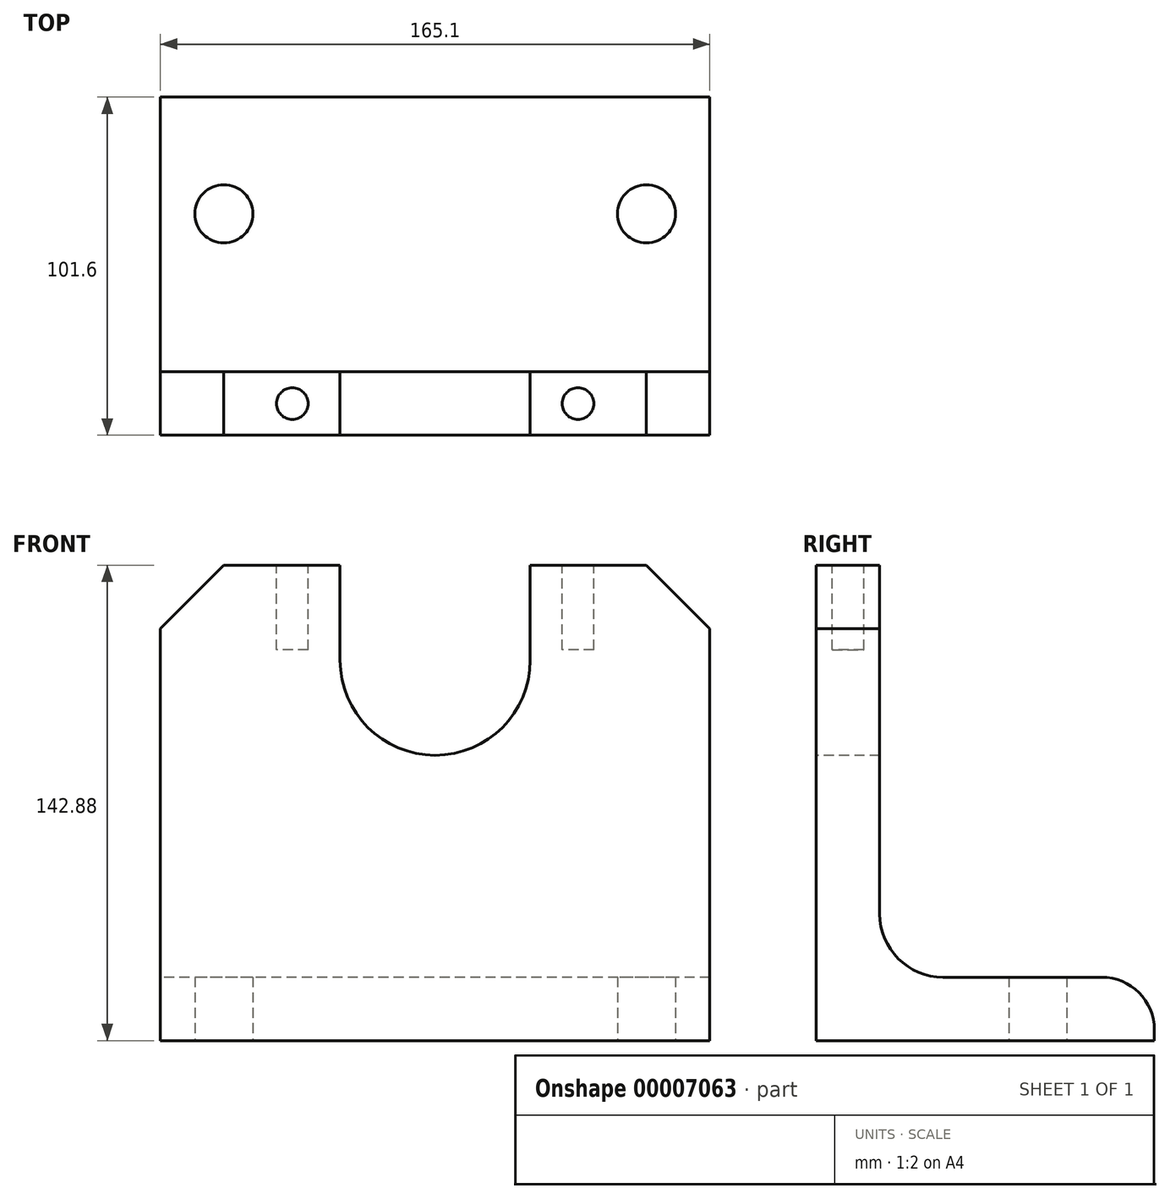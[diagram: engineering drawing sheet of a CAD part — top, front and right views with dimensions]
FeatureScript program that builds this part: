
annotation { "Feature Type Name" : "Feature", "Feature Type Description" : "" }
export const myFeature = defineFeature(function(context is Context, id is Id, definition is map)
    precondition{}
    {
        {
            var Q0;
            Q0=qCreatedBy(makeId("Right.planeOp"),FACE);
            var sketch = newSketch(context, id + "F0", { "sketchPlane" : qUnion([Q0])});
            skLineSegment(sketch, "E0", {"start": v(0, 0) * mm, "end": v(101.6, 0) * mm});
            skLineSegment(sketch, "E1", {"start": v(0, 0) * mm, "end": v(0, 142.88) * mm});
            skLineSegment(sketch, "E2.0", {"start": v(38.1, 19.05) * mm, "end": v(85.73, 19.05) * mm});
            skLineSegment(sketch, "E3.0", {"start": v(19.05, 38.1) * mm, "end": v(19.05, 142.88) * mm});
            skPoint(sketch, "E4.visualSharp", {"position": v(19.05, 19.05) * mm});
            skArc(sketch, "E4.filletArc", {"start": v(19.05, 38.1) * mm, "mid": v(24.63, 24.63) * mm, "end": v(38.1, 19.05) * mm});
            skLineSegment(sketch, "E5", {"start": v(101.6, 0) * mm, "end": v(101.6, 3.18) * mm});
            skArc(sketch, "E6.filletArc", {"start": v(101.6, 3.18) * mm, "mid": v(96.95, 14.4) * mm, "end": v(85.73, 19.05) * mm});
            skLineSegment(sketch, "E7", {"start": v(0, 142.88) * mm, "end": v(19.05, 142.88) * mm});
            skSolve(sketch);
        }
        {
            var Q0;
            Q0 = qSketchRegion(id + "F0", true);
            extrude(context, id + "F1", {"entities" : qUnion([Q0]), "endBound" : BoundingType.SYMMETRIC, "depth" : 165.1 * mm});
        }
        {
            var Q0;
            Q0=makeQuery(id+"F1.opExtrude","CAP_EDGE",EDGE,{"disambiguationData":[OSD([sQuery(id+"F0.wireOp",EDGE,"E7")])],"isStart":false});
            var Q1;
            Q1=makeQuery(id+"F1.opExtrude","CAP_EDGE",EDGE,{"disambiguationData":[OSD([sQuery(id+"F0.wireOp",EDGE,"E7")])],"isStart":true});
            chamfer(context, id + "F2", {"entities" : qUnion([Q0, Q1]), "width" : 19.05 * mm, "tangentPropagation" : true});
        }
        {
            var Q0;
            Q0=makeQuery(id+"F1.opExtrude","SWEPT_FACE",FACE,{"disambiguationData":[OSD([sQuery(id+"F0.wireOp",EDGE,"E1")])]});
            var sketch = newSketch(context, id + "F3", { "sketchPlane" : qUnion([Q0])});
            skLineSegment(sketch, "E8", {"start": v(0, 142.88) * mm, "end": v(0, 0) * mm, "construction": true});
            skLineSegment(sketch, "E9.0", {"start": v(82.55, 114.3) * mm, "end": v(-82.55, 114.3) * mm, "construction": true});
            skArc(sketch, "E10", {"start": v(-28.58, 114.3) * mm, "mid": v(0, 85.73) * mm, "end": v(28.58, 114.3) * mm});
            skLineSegment(sketch, "E11", {"start": v(-28.58, 114.3) * mm, "end": v(-28.58, 200.77) * mm});
            skLineSegment(sketch, "E12", {"start": v(28.58, 114.3) * mm, "end": v(28.58, 203.32) * mm});
            skLineSegment(sketch, "E13", {"start": v(28.58, 203.32) * mm, "end": v(-28.58, 200.77) * mm});
            skSolve(sketch);
        }
        {
            var Q0;
            {var subQ3=sQuery(id+"F3.wireOp",EDGE,"E10");Q0=makeQuery(id+"F3.imprint","IMPRINT",FACE,{"disambiguationData":[TD([[makeQuery(id+"F3.imprint","IMPRINT",EDGE,{"derivedFrom":subQ3}),1.0]])]});}
            extrude(context, id + "F4", {"entities" : qUnion([Q0]), "operationType" : NewBodyOperationType.REMOVE, "endBound" : BoundingType.THROUGH_ALL, "oppositeDirection" : true, "depth" : 25.4 * mm});
        }
        {
            var Q0;
            {var subQ0=sQuery(id+"F0.wireOp",EDGE,"E7");Q0=makeQuery(id+"F4.boolean.opBoolean","SPLIT",FACE,{"disambiguationData":[TD([makeQuery(id+"F4.opExtrude","SWEPT_FACE",FACE,{"disambiguationData":[OSD([sQuery(id+"F3.wireOp",EDGE,"E11")])]})])],"derivedFrom":makeQuery(id+"F1.opExtrude","SWEPT_FACE",FACE,{"disambiguationData":[OSD([subQ0])]})});}
            var sketch = newSketch(context, id + "F5", { "sketchPlane" : qUnion([Q0])});
            skLineSegment(sketch, "E14", {"start": v(-63.5, 9.53) * mm, "end": v(0, 9.53) * mm, "construction": true});
            skLineSegment(sketch, "E15", {"start": v(0, -48.73) * mm, "end": v(0, 119.35) * mm, "construction": true});
            skLineSegment(sketch, "E16.0", {"start": v(-42.93, -48.73) * mm, "end": v(-42.93, 119.35) * mm, "construction": true});
            skCircle(sketch, "E17", {"center": v(-42.93, 9.52) * mm, "radius": 4.76 * mm});
            skCircle(sketch, "E18.0.MirrorC", {"center": v(42.93, 9.52) * mm, "radius": 4.76 * mm});
            skSolve(sketch);
        }
        {
            var Q0;
            Q0 = qSketchRegion(id + "F5", true);
            extrude(context, id + "F6", {"entities" : qUnion([Q0]), "operationType" : NewBodyOperationType.REMOVE, "oppositeDirection" : true, "depth" : 25.4 * mm});
        }
        {
            var Q0;
            Q0=makeQuery(id+"F1.opExtrude","SWEPT_FACE",FACE,{"disambiguationData":[OSD([sQuery(id+"F0.wireOp",EDGE,"E0")])]});
            var sketch = newSketch(context, id + "F7", { "sketchPlane" : qUnion([Q0])});
            skLineSegment(sketch, "E19.0", {"start": v(82.55, 0) * mm, "end": v(-82.55, 0) * mm, "construction": true});
            skLineSegment(sketch, "E20", {"start": v(0, 34.37) * mm, "end": v(0, -116.49) * mm, "construction": true});
            skLineSegment(sketch, "E21.0", {"start": v(82.55, -66.55) * mm, "end": v(-82.55, -66.55) * mm, "construction": true});
            skLineSegment(sketch, "E22.0", {"start": v(63.5, 34.37) * mm, "end": v(63.5, -116.49) * mm, "construction": true});
            skCircle(sketch, "E23", {"center": v(63.5, -66.55) * mm, "radius": 8.73 * mm});
            skCircle(sketch, "E24.0.MirrorC", {"center": v(-63.5, -66.55) * mm, "radius": 8.73 * mm});
            skSolve(sketch);
        }
        {
            var Q0;
            Q0 = qSketchRegion(id + "F7", true);
            extrude(context, id + "F8", {"entities" : qUnion([Q0]), "operationType" : NewBodyOperationType.REMOVE, "endBound" : BoundingType.THROUGH_ALL, "oppositeDirection" : true, "depth" : 25.4 * mm});
        }
    });
